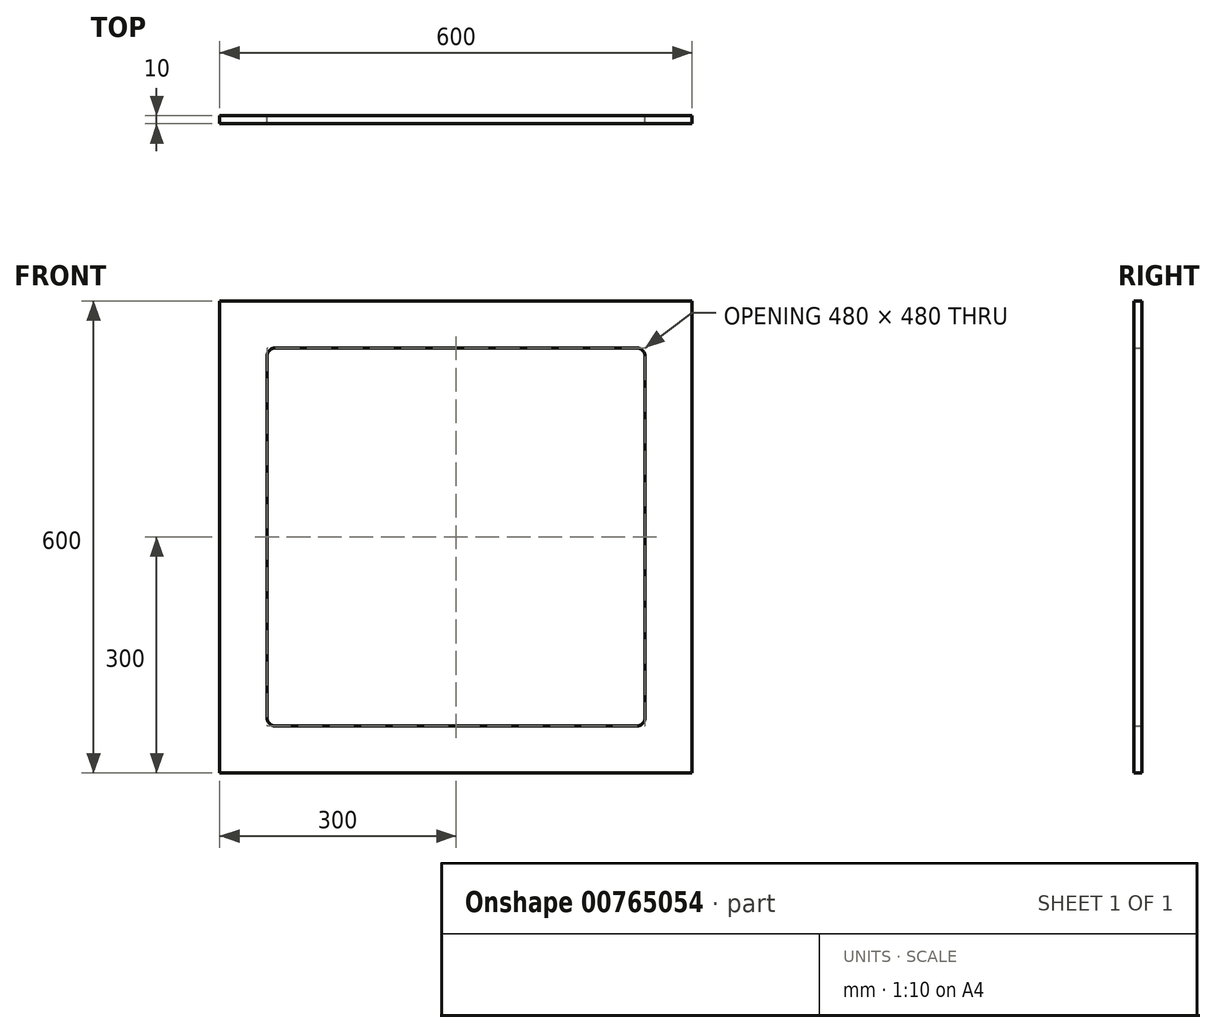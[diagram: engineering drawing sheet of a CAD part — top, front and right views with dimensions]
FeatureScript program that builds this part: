
annotation { "Feature Type Name" : "Feature", "Feature Type Description" : "" }
export const myFeature = defineFeature(function(context is Context, id is Id, definition is map)
    precondition{}
    {
        {
            var Q0;
            Q0=qCreatedBy(makeId("Front.planeOp"),FACE);
            var sketch = newSketch(context, id + "F0", { "sketchPlane" : qUnion([Q0])});
            skLineSegment(sketch, "E0.bottom", {"start": v(0, 0) * mm, "end": v(600, 0) * mm});
            skLineSegment(sketch, "E0.top", {"start": v(0, 600) * mm, "end": v(600, 600) * mm});
            skLineSegment(sketch, "E0.left", {"start": v(0, 0) * mm, "end": v(0, 600) * mm});
            skLineSegment(sketch, "E0.right", {"start": v(600, 0) * mm, "end": v(600, 600) * mm});
            skLineSegment(sketch, "E1.bottom", {"start": v(70, 540) * mm, "end": v(530, 540) * mm});
            skLineSegment(sketch, "E1.top", {"start": v(70, 60) * mm, "end": v(530, 60) * mm});
            skLineSegment(sketch, "E1.left", {"start": v(60, 530) * mm, "end": v(60, 70) * mm});
            skLineSegment(sketch, "E1.right", {"start": v(540, 530) * mm, "end": v(540, 70) * mm});
            skPoint(sketch, "E2.visualSharp", {"position": v(60, 540) * mm});
            skArc(sketch, "E2.filletArc", {"start": v(70, 540) * mm, "mid": v(62.93, 537.07) * mm, "end": v(60, 530) * mm});
            skPoint(sketch, "E3.visualSharp", {"position": v(540, 540) * mm});
            skArc(sketch, "E3.filletArc", {"start": v(540, 530) * mm, "mid": v(537.07, 537.07) * mm, "end": v(530, 540) * mm});
            skPoint(sketch, "E4.visualSharp", {"position": v(540, 60) * mm});
            skArc(sketch, "E4.filletArc", {"start": v(530, 60) * mm, "mid": v(537.07, 62.93) * mm, "end": v(540, 70) * mm});
            skPoint(sketch, "E5.visualSharp", {"position": v(60, 60) * mm});
            skArc(sketch, "E5.filletArc", {"start": v(60, 70) * mm, "mid": v(62.93, 62.93) * mm, "end": v(70, 60) * mm});
            skSolve(sketch);
        }
        {
            var Q0;
            Q0 = qSketchRegion(id + "F0", true);
            extrude(context, id + "F1", {"entities" : qUnion([Q0]), "depth" : 10 * mm, "offsetDistance" : 25 * mm});
        }
    });
